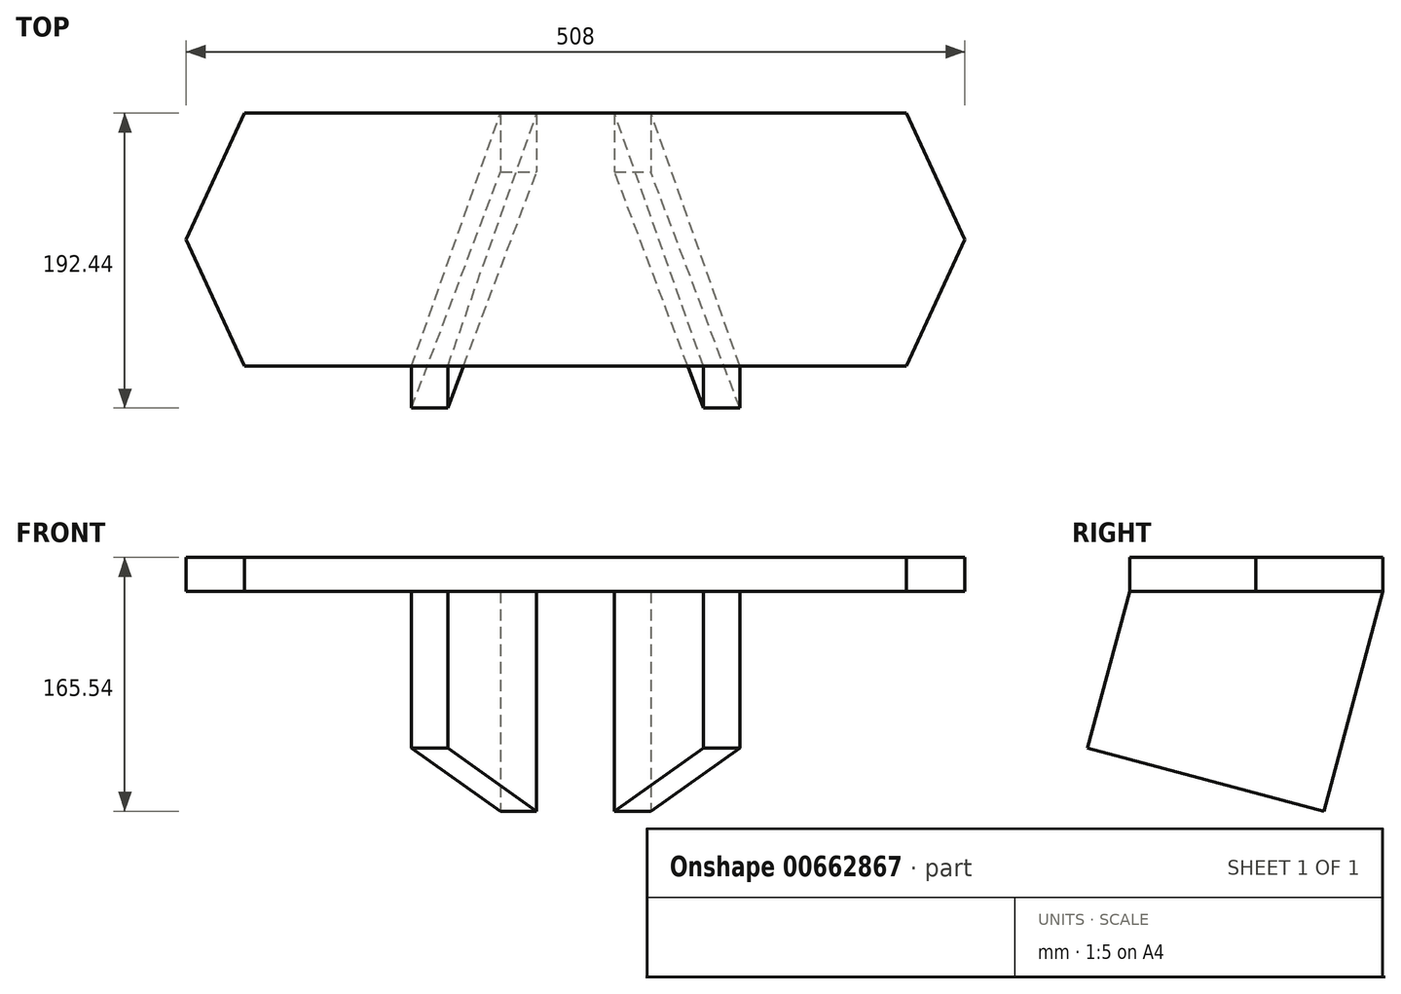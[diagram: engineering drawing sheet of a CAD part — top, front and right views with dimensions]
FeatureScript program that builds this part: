
annotation { "Feature Type Name" : "Feature", "Feature Type Description" : "" }
export const myFeature = defineFeature(function(context is Context, id is Id, definition is map)
    precondition{}
    {
        {
            var Q0;
            Q0=qCreatedBy(makeId("Top.planeOp"),FACE);
            var sketch = newSketch(context, id + "F0", { "sketchPlane" : qUnion([Q0])});
            skLineSegment(sketch, "E0.bottom", {"start": v(-215.9, 82.55) * mm, "end": v(215.9, 82.55) * mm});
            skLineSegment(sketch, "E0.top", {"start": v(-215.9, -82.55) * mm, "end": v(215.9, -82.55) * mm});
            skPoint(sketch, "E0.middle", {"position": v(0, 0) * mm});
            skLineSegment(sketch, "E1", {"start": v(-254, 0) * mm, "end": v(-215.9, -82.55) * mm});
            skLineSegment(sketch, "E2", {"start": v(-254, 0) * mm, "end": v(-215.9, 82.55) * mm});
            skPoint(sketch, "E3.orphan", {"position": v(-254, 82.55) * mm});
            skPoint(sketch, "E4.orphan", {"position": v(-254, -82.55) * mm});
            skLineSegment(sketch, "E5.MirrorCS", {"start": v(254, 0) * mm, "end": v(215.9, 82.55) * mm});
            skLineSegment(sketch, "E6.MirrorCS", {"start": v(254, 0) * mm, "end": v(215.9, -82.55) * mm});
            skPoint(sketch, "E7.orphan", {"position": v(254, 82.55) * mm});
            skPoint(sketch, "E8.orphan", {"position": v(254, -82.55) * mm});
            skLineSegment(sketch, "E9", {"start": v(-215.9, -82.55) * mm, "end": v(215.9, 82.55) * mm, "construction": true});
            skLineSegment(sketch, "E10", {"start": v(215.9, -82.55) * mm, "end": v(-215.9, 82.55) * mm, "construction": true});
            skLineSegment(sketch, "E11", {"start": v(215.9, 82.55) * mm, "end": v(215.9, -82.55) * mm, "construction": true});
            skLineSegment(sketch, "E12", {"start": v(-215.9, -82.55) * mm, "end": v(-215.9, 82.55) * mm, "construction": true});
            skLineSegment(sketch, "E13", {"start": v(215.9, 0) * mm, "end": v(-215.9, 0) * mm, "construction": true});
            skSolve(sketch);
        }
        {
            var Q0;
            Q0 = qSketchRegion(id + "F0", true);
            extrude(context, id + "F1", {"entities" : qUnion([Q0]), "depth" : 22.22 * mm, "offsetDistance" : 25.4 * mm});
        }
        {
            var Q0;
            Q0=sQuery(id+"F0.wireOp",EDGE,"E13");
            cPlane(context, id + "F2", {"entities" : qUnion([Q0]), "cplaneType" : CPlaneType.LINE_ANGLE, "offset" : 25.4 * mm, "angle" : 105 * degree, "width" : 152.4 * mm, "height" : 152.4 * mm});
        }
        {
            var Q0;
            Q0=qCreatedBy(id+"F2.planeOp",FACE);
            cPlane(context, id + "F3", {"entities" : qUnion([Q0]), "cplaneType" : CPlaneType.OFFSET, "offset" : 127 * mm, "oppositeDirection" : true, "width" : 152.4 * mm, "height" : 152.4 * mm});
        }
        {
            var Q0;
            Q0=qCreatedBy(id+"F3.planeOp",FACE);
            var sketch = newSketch(context, id + "F4", { "sketchPlane" : qUnion([Q0])});
            skLineSegment(sketch, "E14.0", {"start": v(-122.68, 79.74) * mm, "end": v(-99.03, 79.74) * mm});
            skLineSegment(sketch, "E15.0", {"start": v(-63.5, -79.74) * mm, "end": v(-39.85, -79.74) * mm});
            skLineSegment(sketch, "E16.trimOffspring", {"start": v(99.03, 79.74) * mm, "end": v(122.68, 79.74) * mm});
            skLineSegment(sketch, "E17.trimOffspring", {"start": v(39.85, -79.74) * mm, "end": v(63.5, -79.74) * mm});
            skPoint(sketch, "E18.orphan", {"position": v(-215.9, -79.74) * mm});
            skPoint(sketch, "E19.orphan", {"position": v(-215.9, 79.74) * mm});
            skPoint(sketch, "E20.orphan", {"position": v(215.9, 79.74) * mm});
            skPoint(sketch, "E21.orphan", {"position": v(215.9, -79.74) * mm});
            skLineSegment(sketch, "E22.0", {"start": v(-215.9, -79.74) * mm, "end": v(-39.85, -79.74) * mm});
            skLineSegment(sketch, "E23.0", {"start": v(-215.9, 79.74) * mm, "end": v(-25.4, 79.74) * mm});
            skLineSegment(sketch, "E24", {"start": v(-107.1, -79.74) * mm, "end": v(-49.05, 79.74) * mm});
            skLineSegment(sketch, "E25", {"start": v(-83.44, -79.74) * mm, "end": v(-25.4, 79.74) * mm});
            skLineSegment(sketch, "E26.MirrorCS", {"start": v(83.44, -79.74) * mm, "end": v(25.4, 79.74) * mm});
            skLineSegment(sketch, "E27.MirrorCS", {"start": v(107.1, -79.74) * mm, "end": v(49.05, 79.74) * mm});
            skLineSegment(sketch, "E28.trimOffspring", {"start": v(39.85, -79.74) * mm, "end": v(215.9, -79.74) * mm});
            skLineSegment(sketch, "E29.trimOffspring", {"start": v(25.4, 79.74) * mm, "end": v(215.9, 79.74) * mm});
            skSolve(sketch);
        }
        {
            var Q0;
            Q0 = qSketchRegion(id + "F4", true);
            extrude(context, id + "F5", {"entities" : qUnion([Q0]), "endBound" : BoundingType.UP_TO_NEXT, "depth" : 127 * mm, "offsetDistance" : 25.4 * mm});
        }
    });
